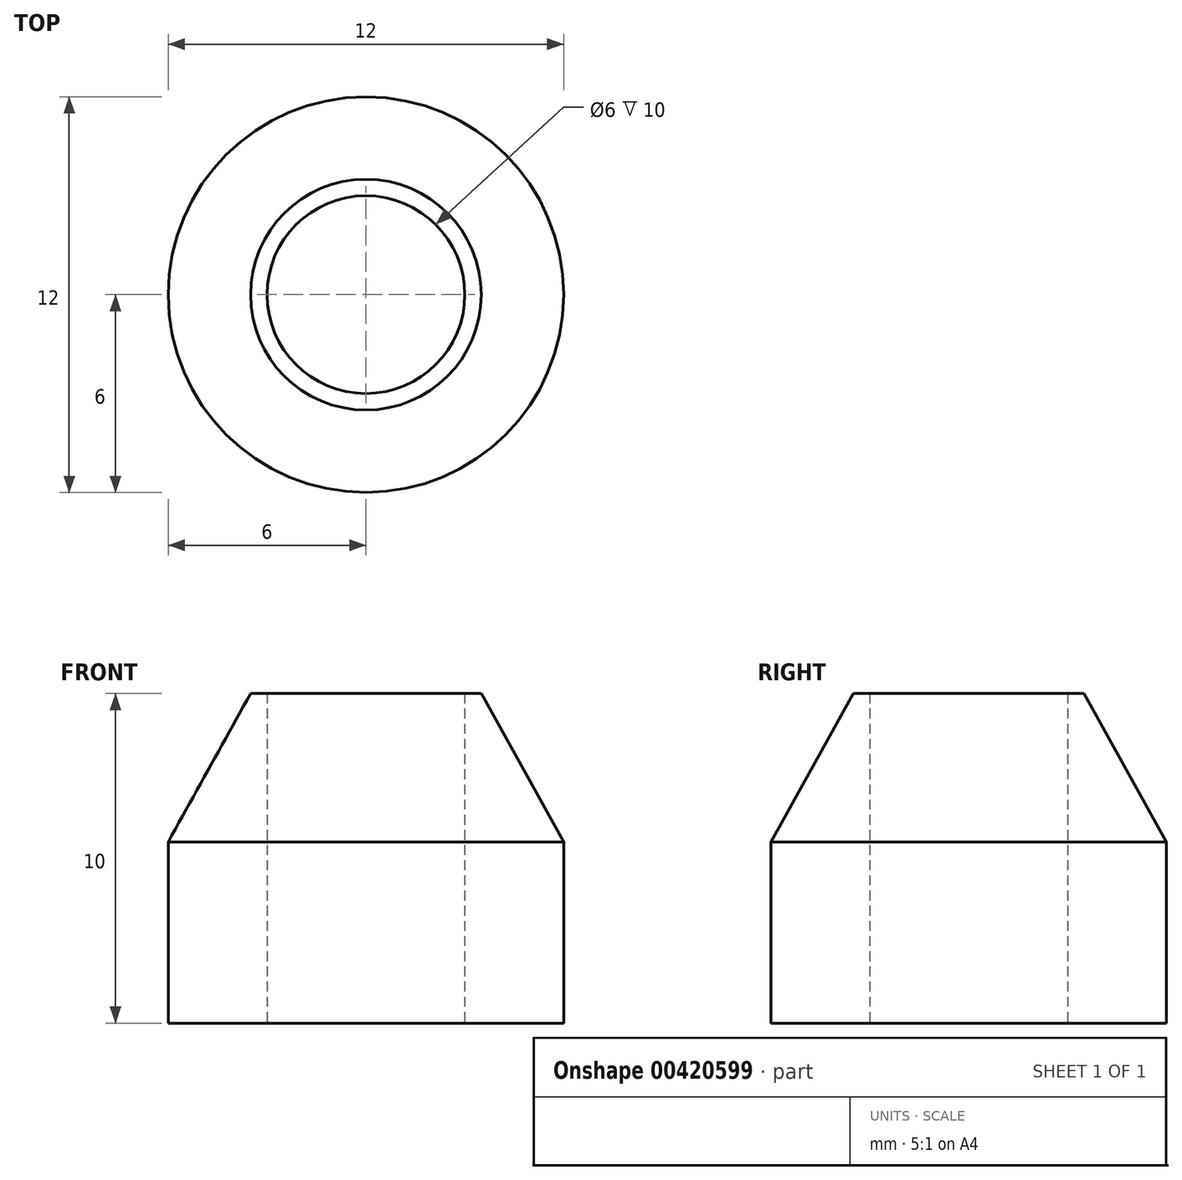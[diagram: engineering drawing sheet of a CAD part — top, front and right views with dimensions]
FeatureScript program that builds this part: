
annotation { "Feature Type Name" : "Feature", "Feature Type Description" : "" }
export const myFeature = defineFeature(function(context is Context, id is Id, definition is map)
    precondition{}
    {
        {
            var Q0;
            Q0=qCreatedBy(makeId("Front.planeOp"),FACE);
            var sketch = newSketch(context, id + "F0", { "sketchPlane" : qUnion([Q0])});
            skLineSegment(sketch, "E0", {"start": v(0, 0) * mm, "end": v(0, 15.05) * mm, "construction": true});
            skLineSegment(sketch, "E1", {"start": v(-3, 0) * mm, "end": v(-3, 10) * mm});
            skLineSegment(sketch, "E2", {"start": v(-3, 10) * mm, "end": v(-3.5, 10) * mm});
            skLineSegment(sketch, "E3", {"start": v(-3.5, 10) * mm, "end": v(-6, 5.5) * mm});
            skLineSegment(sketch, "E4", {"start": v(-6, 5.5) * mm, "end": v(-6, 0) * mm});
            skLineSegment(sketch, "E5", {"start": v(-6, 0) * mm, "end": v(-3, 0) * mm});
            skSolve(sketch);
        }
        {
            var Q0;
            Q0 = qSketchRegion(id + "F0", true);
            var Q1;
            Q1=sQuery(id+"F0.wireOp",EDGE,"E0");
            revolve(context, id + "F1", {"entities" : qUnion([Q0]), "axis" : qUnion([Q1]), "revolveType" : RevolveType.FULL});
        }
    });
